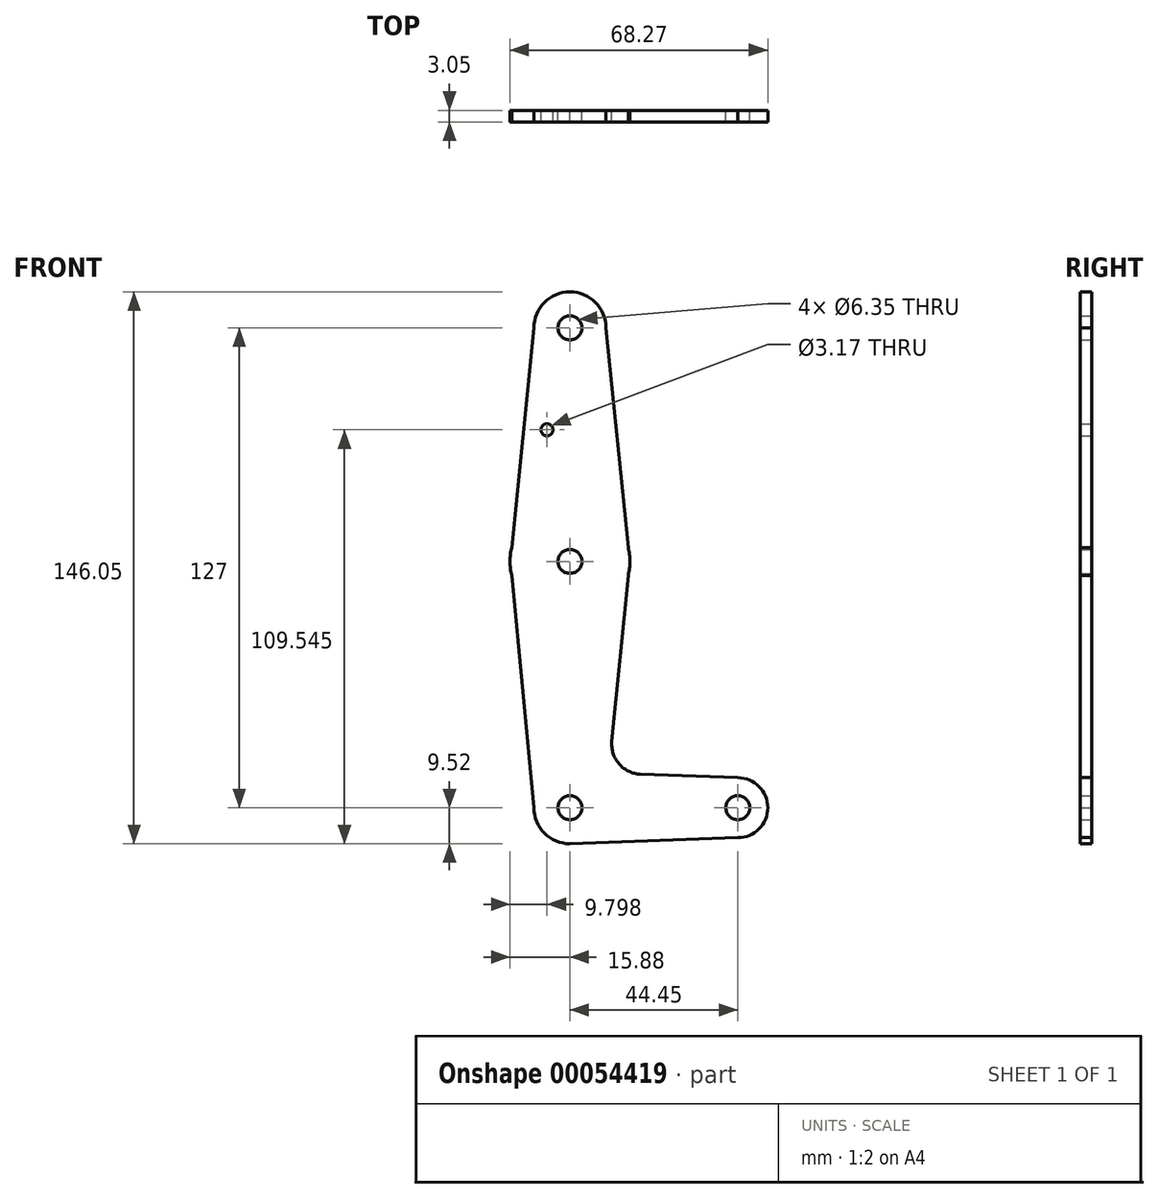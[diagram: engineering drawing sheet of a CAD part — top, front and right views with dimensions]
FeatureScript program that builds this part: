
annotation { "Feature Type Name" : "Feature", "Feature Type Description" : "" }
export const myFeature = defineFeature(function(context is Context, id is Id, definition is map)
    precondition{}
    {
        {
            var Q0;
            Q0=qCreatedBy(makeId("Front.planeOp"),FACE);
            var sketch = newSketch(context, id + "F0", { "sketchPlane" : qUnion([Q0])});
            skCircle(sketch, "E0", {"center": v(0, 95.04) * mm, "radius": 9.53 * mm});
            skCircle(sketch, "E1", {"center": v(0, 33.23) * mm, "radius": 15.88 * mm});
            skCircle(sketch, "E2", {"center": v(0, -31.96) * mm, "radius": 9.53 * mm});
            skCircle(sketch, "E3", {"center": v(44.45, -31.96) * mm, "radius": 7.94 * mm});
            skLineSegment(sketch, "E4", {"start": v(0, 95.04) * mm, "end": v(0, 31.54) * mm, "construction": true});
            skLineSegment(sketch, "E5", {"start": v(0, 31.54) * mm, "end": v(0, -31.96) * mm, "construction": true});
            skLineSegment(sketch, "E6", {"start": v(0, -31.96) * mm, "end": v(44.45, -31.96) * mm, "construction": true});
            skLineSegment(sketch, "E7", {"start": v(-9.53, 95.04) * mm, "end": v(-15.44, 36.9) * mm});
            skLineSegment(sketch, "E8", {"start": v(-9.52, -31.96) * mm, "end": v(-15.44, 29.55) * mm});
            skLineSegment(sketch, "E9", {"start": v(11.1, -14.39) * mm, "end": v(15.44, 29.55) * mm});
            skLineSegment(sketch, "E10", {"start": v(15.44, 36.9) * mm, "end": v(9.53, 95.04) * mm});
            skLineSegment(sketch, "E11", {"start": v(44.45, -24.02) * mm, "end": v(18.71, -23.1) * mm});
            skLineSegment(sketch, "E12", {"start": v(0, -41.48) * mm, "end": v(44.45, -39.9) * mm});
            skCircle(sketch, "E13", {"center": v(-6.08, 68.07) * mm, "radius": 1.59 * mm});
            skCircle(sketch, "E14", {"center": v(0, 95.04) * mm, "radius": 3.18 * mm});
            skCircle(sketch, "E15", {"center": v(0, -31.96) * mm, "radius": 3.18 * mm});
            skCircle(sketch, "E16", {"center": v(44.45, -31.96) * mm, "radius": 3.18 * mm});
            skCircle(sketch, "E17", {"center": v(0, 33.23) * mm, "radius": 3.18 * mm});
            skArc(sketch, "E18.filletArc", {"start": v(11.1, -14.39) * mm, "mid": v(13.02, -20.4) * mm, "end": v(18.71, -23.1) * mm});
            skSolve(sketch);
        }
        {
            var Q0;
            {var subQ1=sQuery(id+"F0.wireOp",EDGE,"E7");Q0=makeQuery(id+"F0.imprint","IMPRINT",FACE,{"disambiguationData":[TD([[makeQuery(id+"F0.imprint","IMPRINT",EDGE,{"derivedFrom":subQ1}),1.0]])]});}
            var Q1;
            Q1=makeQuery(id+"F0.imprint","IMPRINT",FACE,{"disambiguationData":[TD([[makeQuery(id+"F0.imprint","IMPRINT",EDGE,{"derivedFrom":sQuery(id+"F0.wireOp",EDGE,"E14")}),-1.0]])]});
            var Q2;
            Q2=makeQuery(id+"F0.imprint","IMPRINT",FACE,{"disambiguationData":[TD([[makeQuery(id+"F0.imprint","IMPRINT",EDGE,{"derivedFrom":sQuery(id+"F0.wireOp",EDGE,"E17")}),-1.0]])]});
            var Q3;
            Q3=makeQuery(id+"F0.imprint","IMPRINT",FACE,{"disambiguationData":[TD([[makeQuery(id+"F0.imprint","IMPRINT",EDGE,{"derivedFrom":sQuery(id+"F0.wireOp",EDGE,"E15")}),-1.0]])]});
            var Q4;
            Q4=makeQuery(id+"F0.imprint","IMPRINT",FACE,{"disambiguationData":[TD([[makeQuery(id+"F0.imprint","IMPRINT",EDGE,{"derivedFrom":sQuery(id+"F0.wireOp",EDGE,"E16")}),-1.0]])]});
            var Q5;
            {var subQ0=sQuery(id+"F0.wireOp",EDGE,"E8");Q5=makeQuery(id+"F0.imprint","IMPRINT",FACE,{"disambiguationData":[TD([[makeQuery(id+"F0.imprint","IMPRINT",EDGE,{"derivedFrom":subQ0}),-1.0]])]});}
            extrude(context, id + "F1", {"entities" : qUnion([Q0, Q1, Q2, Q3, Q4, Q5]), "depth" : 3.05 * mm});
        }
    });
